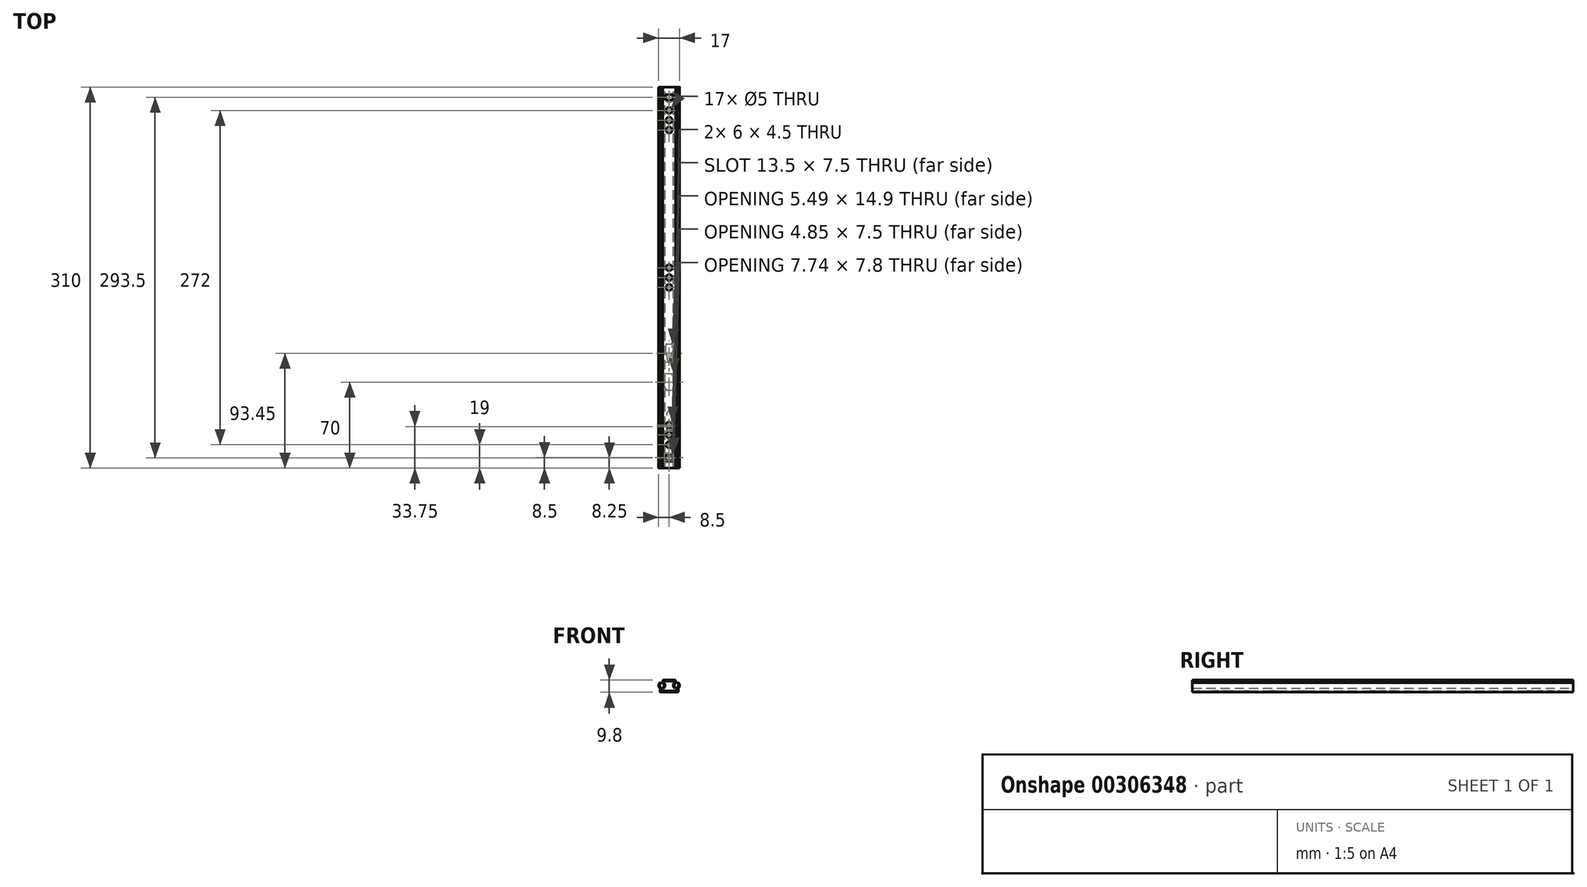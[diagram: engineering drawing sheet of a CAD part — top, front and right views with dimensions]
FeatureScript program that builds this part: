
annotation { "Feature Type Name" : "Feature", "Feature Type Description" : "" }
export const myFeature = defineFeature(function(context is Context, id is Id, definition is map)
    precondition{}
    {
        {
            var Q0;
            Q0=qCreatedBy(makeId("Front.planeOp"),FACE);
            var sketch = newSketch(context, id + "F0", { "sketchPlane" : qUnion([Q0])});
            skLineSegment(sketch, "E0", {"start": v(0, 0) * mm, "end": v(6.95, 0) * mm});
            skLineSegment(sketch, "E1", {"start": v(7.45, 0.5) * mm, "end": v(7.45, 3.02) * mm});
            skLineSegment(sketch, "E2", {"start": v(6.55, 3.43) * mm, "end": v(6.55, 1.4) * mm});
            skLineSegment(sketch, "E3", {"start": v(6.05, 0.9) * mm, "end": v(0, 0.9) * mm});
            skLineSegment(sketch, "E4", {"start": v(0, 0) * mm, "end": v(0, 0.9) * mm, "construction": true});
            skArc(sketch, "E5", {"start": v(7.6, 3.38) * mm, "mid": v(8.5, 5.55) * mm, "end": v(7.56, 7.7) * mm});
            skArc(sketch, "E6", {"start": v(6.75, 3.83) * mm, "mid": v(7.6, 5.48) * mm, "end": v(6.81, 7.16) * mm});
            skLineSegment(sketch, "E7", {"start": v(7.33, 7.74) * mm, "end": v(6.85, 7.5) * mm});
            skLineSegment(sketch, "E8.MirrorCS", {"start": v(-7.33, 7.74) * mm, "end": v(-6.85, 7.5) * mm});
            skLineSegment(sketch, "E9.MirrorCS", {"start": v(-7.45, 0.5) * mm, "end": v(-7.45, 3.02) * mm});
            skLineSegment(sketch, "E10.MirrorCS", {"start": v(-6.55, 3.43) * mm, "end": v(-6.55, 1.4) * mm});
            skLineSegment(sketch, "E11.MirrorCS", {"start": v(-6.05, 0.9) * mm, "end": v(0, 0.9) * mm});
            skArc(sketch, "E12.MirrorCS", {"start": v(-7.6, 3.38) * mm, "mid": v(-8.5, 5.55) * mm, "end": v(-7.56, 7.7) * mm});
            skArc(sketch, "E13.MirrorCS", {"start": v(-6.75, 3.83) * mm, "mid": v(-7.6, 5.48) * mm, "end": v(-6.81, 7.16) * mm});
            skLineSegment(sketch, "E14.MirrorCS", {"start": v(0, 0) * mm, "end": v(-6.95, 0) * mm});
            skLineSegment(sketch, "E15", {"start": v(6.55, 3.7) * mm, "end": v(7.45, 3.24) * mm, "construction": true});
            skLineSegment(sketch, "E16", {"start": v(5.5, 5.52) * mm, "end": v(-5.5, 5.52) * mm, "construction": true});
            skLineSegment(sketch, "E17", {"start": v(6.55, 0.9) * mm, "end": v(7.45, 0.9) * mm, "construction": true});
            skLineSegment(sketch, "E18", {"start": v(7.6, 5.52) * mm, "end": v(8.5, 5.52) * mm, "construction": true});
            skPoint(sketch, "E19.visualSharp", {"position": v(6.55, 0.9) * mm});
            skArc(sketch, "E19.filletArc", {"start": v(6.05, 0.9) * mm, "mid": v(6.4, 1.05) * mm, "end": v(6.55, 1.4) * mm});
            skPoint(sketch, "E20.visualSharp", {"position": v(7.45, 0) * mm});
            skArc(sketch, "E20.filletArc", {"start": v(6.95, 0) * mm, "mid": v(7.3, 0.15) * mm, "end": v(7.45, 0.5) * mm});
            skPoint(sketch, "E21.visualSharp", {"position": v(-6.55, 0.9) * mm});
            skArc(sketch, "E21.filletArc", {"start": v(-6.55, 1.4) * mm, "mid": v(-6.4, 1.05) * mm, "end": v(-6.05, 0.9) * mm});
            skPoint(sketch, "E22.visualSharp", {"position": v(-7.45, 0) * mm});
            skArc(sketch, "E22.filletArc", {"start": v(-7.45, 0.5) * mm, "mid": v(-7.3, 0.15) * mm, "end": v(-6.95, 0) * mm});
            skPoint(sketch, "E23.visualSharp", {"position": v(7.45, 3.24) * mm});
            skArc(sketch, "E23.filletArc", {"start": v(7.6, 3.38) * mm, "mid": v(7.49, 3.21) * mm, "end": v(7.45, 3.02) * mm});
            skPoint(sketch, "E24.visualSharp", {"position": v(6.55, 3.7) * mm});
            skArc(sketch, "E24.filletArc", {"start": v(6.75, 3.83) * mm, "mid": v(6.6, 3.66) * mm, "end": v(6.55, 3.43) * mm});
            skPoint(sketch, "E25.visualSharp", {"position": v(-7.45, 3.24) * mm});
            skArc(sketch, "E25.filletArc", {"start": v(-7.45, 3.02) * mm, "mid": v(-7.49, 3.21) * mm, "end": v(-7.6, 3.38) * mm});
            skPoint(sketch, "E26.visualSharp", {"position": v(-6.55, 3.7) * mm});
            skArc(sketch, "E26.filletArc", {"start": v(-6.55, 3.43) * mm, "mid": v(-6.6, 3.66) * mm, "end": v(-6.75, 3.83) * mm});
            skPoint(sketch, "E27.visualSharp", {"position": v(6.55, 7.34) * mm});
            skArc(sketch, "E27.filletArc", {"start": v(6.85, 7.5) * mm, "mid": v(6.74, 7.33) * mm, "end": v(6.81, 7.16) * mm});
            skPoint(sketch, "E28.visualSharp", {"position": v(-6.55, 7.34) * mm});
            skArc(sketch, "E28.filletArc", {"start": v(-6.81, 7.16) * mm, "mid": v(-6.74, 7.33) * mm, "end": v(-6.85, 7.5) * mm});
            skPoint(sketch, "E29.visualSharp", {"position": v(7.45, 7.8) * mm});
            skArc(sketch, "E29.filletArc", {"start": v(7.56, 7.7) * mm, "mid": v(7.45, 7.76) * mm, "end": v(7.33, 7.74) * mm});
            skPoint(sketch, "E30.visualSharp", {"position": v(-7.45, 7.8) * mm});
            skArc(sketch, "E30.filletArc", {"start": v(-7.33, 7.74) * mm, "mid": v(-7.45, 7.76) * mm, "end": v(-7.56, 7.7) * mm});
            skLineSegment(sketch, "E31", {"start": v(0, 9.8) * mm, "end": v(4.75, 9.8) * mm});
            skLineSegment(sketch, "E32", {"start": v(5.25, 9.3) * mm, "end": v(5.25, 7.6) * mm});
            skArc(sketch, "E33", {"start": v(5.05, 7.2) * mm, "mid": v(4.2, 5.56) * mm, "end": v(4.99, 3.88) * mm});
            skLineSegment(sketch, "E34", {"start": v(4.47, 3.3) * mm, "end": v(4.95, 3.55) * mm});
            skLineSegment(sketch, "E35", {"start": v(4.35, 7.8) * mm, "end": v(5.25, 7.34) * mm, "construction": true});
            skLineSegment(sketch, "E36", {"start": v(4.35, 8.02) * mm, "end": v(4.35, 8.4) * mm});
            skLineSegment(sketch, "E37", {"start": v(3.85, 8.9) * mm, "end": v(0, 8.9) * mm});
            skLineSegment(sketch, "E38", {"start": v(3.3, 5.52) * mm, "end": v(5.5, 5.52) * mm, "construction": true});
            skLineSegment(sketch, "E39", {"start": v(4.35, 8.9) * mm, "end": v(5.25, 8.9) * mm, "construction": true});
            skLineSegment(sketch, "E40", {"start": v(0, 9.8) * mm, "end": v(0, 8.9) * mm, "construction": true});
            skLineSegment(sketch, "E41", {"start": v(3.3, 5.52) * mm, "end": v(4.2, 5.52) * mm, "construction": true});
            skArc(sketch, "E42", {"start": v(4.2, 7.66) * mm, "mid": v(3.3, 5.49) * mm, "end": v(4.24, 3.33) * mm});
            skPoint(sketch, "E43.visualSharp", {"position": v(4.35, 8.9) * mm});
            skArc(sketch, "E43.filletArc", {"start": v(4.35, 8.4) * mm, "mid": v(4.2, 8.75) * mm, "end": v(3.85, 8.9) * mm});
            skPoint(sketch, "E44.visualSharp", {"position": v(5.25, 9.8) * mm});
            skArc(sketch, "E44.filletArc", {"start": v(5.25, 9.3) * mm, "mid": v(5.1, 9.65) * mm, "end": v(4.75, 9.8) * mm});
            skPoint(sketch, "E45.visualSharp", {"position": v(5.25, 7.34) * mm});
            skArc(sketch, "E45.filletArc", {"start": v(5.05, 7.2) * mm, "mid": v(5.2, 7.38) * mm, "end": v(5.25, 7.6) * mm});
            skPoint(sketch, "E46.visualSharp", {"position": v(4.35, 7.8) * mm});
            skArc(sketch, "E46.filletArc", {"start": v(4.2, 7.66) * mm, "mid": v(4.31, 7.83) * mm, "end": v(4.35, 8.02) * mm});
            skPoint(sketch, "E47.visualSharp", {"position": v(5.25, 3.7) * mm});
            skArc(sketch, "E47.filletArc", {"start": v(4.95, 3.55) * mm, "mid": v(5.06, 3.7) * mm, "end": v(4.99, 3.88) * mm});
            skPoint(sketch, "E48.visualSharp", {"position": v(4.35, 3.24) * mm});
            skArc(sketch, "E48.filletArc", {"start": v(4.24, 3.33) * mm, "mid": v(4.35, 3.28) * mm, "end": v(4.47, 3.3) * mm});
            skArc(sketch, "E49.MirrorCS", {"start": v(-4.2, 7.66) * mm, "mid": v(-4.31, 7.83) * mm, "end": v(-4.35, 8.02) * mm});
            skArc(sketch, "E50.MirrorCS", {"start": v(-4.24, 3.33) * mm, "mid": v(-4.35, 3.28) * mm, "end": v(-4.47, 3.3) * mm});
            skLineSegment(sketch, "E51.MirrorCS", {"start": v(-4.35, 8.02) * mm, "end": v(-4.35, 8.4) * mm});
            skArc(sketch, "E52.MirrorCS", {"start": v(-4.35, 8.4) * mm, "mid": v(-4.2, 8.75) * mm, "end": v(-3.85, 8.9) * mm});
            skArc(sketch, "E53.MirrorCS", {"start": v(-4.95, 3.55) * mm, "mid": v(-5.06, 3.7) * mm, "end": v(-4.99, 3.88) * mm});
            skLineSegment(sketch, "E54.MirrorCS", {"start": v(-4.47, 3.3) * mm, "end": v(-4.95, 3.55) * mm});
            skArc(sketch, "E55.MirrorCS", {"start": v(-5.05, 7.2) * mm, "mid": v(-5.2, 7.38) * mm, "end": v(-5.25, 7.6) * mm});
            skLineSegment(sketch, "E56.MirrorCS", {"start": v(-4.35, 7.8) * mm, "end": v(-5.25, 7.34) * mm, "construction": true});
            skArc(sketch, "E57.MirrorCS", {"start": v(-5.25, 9.3) * mm, "mid": v(-5.1, 9.65) * mm, "end": v(-4.75, 9.8) * mm});
            skLineSegment(sketch, "E58.MirrorCS", {"start": v(-3.3, 5.52) * mm, "end": v(-4.2, 5.52) * mm, "construction": true});
            skArc(sketch, "E59.MirrorCS", {"start": v(-4.2, 7.66) * mm, "mid": v(-3.3, 5.49) * mm, "end": v(-4.24, 3.33) * mm});
            skPoint(sketch, "E60.MirrorP", {"position": v(-4.35, 3.24) * mm});
            skPoint(sketch, "E61.MirrorP", {"position": v(-5.25, 7.34) * mm});
            skLineSegment(sketch, "E62.MirrorCS", {"start": v(-4.35, 8.9) * mm, "end": v(-5.25, 8.9) * mm, "construction": true});
            skPoint(sketch, "E63.MirrorP", {"position": v(-4.35, 8.9) * mm});
            skPoint(sketch, "E64.MirrorP", {"position": v(-5.25, 9.8) * mm});
            skLineSegment(sketch, "E65.MirrorCS", {"start": v(0, 9.8) * mm, "end": v(-4.75, 9.8) * mm});
            skPoint(sketch, "E66.MirrorP", {"position": v(-4.35, 7.8) * mm});
            skArc(sketch, "E67.MirrorCS", {"start": v(-5.05, 7.2) * mm, "mid": v(-4.2, 5.56) * mm, "end": v(-4.99, 3.88) * mm});
            skPoint(sketch, "E68.MirrorP", {"position": v(-5.25, 3.7) * mm});
            skLineSegment(sketch, "E69.MirrorCS", {"start": v(-3.85, 8.9) * mm, "end": v(0, 8.9) * mm});
            skLineSegment(sketch, "E70.MirrorCS", {"start": v(-5.25, 9.3) * mm, "end": v(-5.25, 7.6) * mm});
            skLineSegment(sketch, "E71.MirrorCS", {"start": v(-3.3, 5.52) * mm, "end": v(-5.5, 5.52) * mm, "construction": true});
            skSolve(sketch);
        }
        {
            var Q0;
            Q0=makeQuery(id+"F0.imprint","IMPRINT",FACE,{"disambiguationData":[TD([[makeQuery(id+"F0.imprint","IMPRINT",EDGE,{"derivedFrom":sQuery(id+"F0.wireOp",EDGE,"E0")}),1.0]])]});
            extrude(context, id + "F1", {"entities" : qUnion([Q0]), "depth" : 310 * mm});
        }
        {
            var Q0;
            Q0=makeQuery(id+"F1.opExtrude","SWEPT_FACE",FACE,{"disambiguationData":[OSD([sQuery(id+"F0.wireOp",EDGE,"E0"),sQuery(id+"F0.wireOp",EDGE,"E14.MirrorCS")])]});
            var sketch = newSketch(context, id + "F2", { "sketchPlane" : qUnion([Q0])});
            skLineSegment(sketch, "E72", {"start": v(0, 310) * mm, "end": v(0, 0) * mm, "construction": true});
            skLineSegment(sketch, "E73", {"start": v(0, 155) * mm, "end": v(-6.95, 155) * mm, "construction": true});
            skCircle(sketch, "E74", {"center": v(0, 10) * mm, "radius": 2.65 * mm});
            skCircle(sketch, "E75", {"center": v(0, 301.5) * mm, "radius": 3.9 * mm});
            skCircle(sketch, "E76", {"center": v(0, 278) * mm, "radius": 2 * mm});
            skCircle(sketch, "E77", {"center": v(0, 266) * mm, "radius": 2 * mm});
            skLineSegment(sketch, "E78", {"start": v(0, 243) * mm, "end": v(0, 237) * mm});
            skArc(sketch, "E79.0.startCap", {"start": v(-3.75, 243) * mm, "mid": v(0, 246.75) * mm, "end": v(3.75, 243) * mm});
            skArc(sketch, "E79.0.endCap", {"start": v(3.75, 237) * mm, "mid": v(0, 233.25) * mm, "end": v(-3.75, 237) * mm});
            skLineSegment(sketch, "E79.0.left", {"start": v(3.75, 243) * mm, "end": v(3.75, 237) * mm});
            skLineSegment(sketch, "E79.0.right", {"start": v(-3.75, 243) * mm, "end": v(-3.75, 237) * mm});
            skArc(sketch, "E80", {"start": v(0, 224) * mm, "mid": v(0.66, 223.75) * mm, "end": v(1, 223.13) * mm});
            skLineSegment(sketch, "E81", {"start": v(1, 223.13) * mm, "end": v(2.74, 210.23) * mm});
            skLineSegment(sketch, "E82", {"start": v(1.75, 209.1) * mm, "end": v(0, 209.1) * mm});
            skArc(sketch, "E83.MirrorCS", {"start": v(0, 224) * mm, "mid": v(-0.66, 223.75) * mm, "end": v(-1, 223.13) * mm});
            skLineSegment(sketch, "E84.MirrorCS", {"start": v(-1, 223.13) * mm, "end": v(-2.74, 210.23) * mm});
            skLineSegment(sketch, "E85.MirrorCS", {"start": v(-1.75, 209.1) * mm, "end": v(0, 209.1) * mm});
            skPoint(sketch, "E86.visualSharp", {"position": v(2.9, 209.1) * mm});
            skArc(sketch, "E86.filletArc", {"start": v(1.75, 209.1) * mm, "mid": v(2.5, 209.44) * mm, "end": v(2.74, 210.23) * mm});
            skPoint(sketch, "E87.visualSharp", {"position": v(-2.9, 209.1) * mm});
            skArc(sketch, "E87.filletArc", {"start": v(-2.74, 210.23) * mm, "mid": v(-2.5, 209.44) * mm, "end": v(-1.75, 209.1) * mm});
            skSolve(sketch);
        }
        {
            var Q0;
            Q0 = qSketchRegion(id + "F2", true);
            extrude(context, id + "F3", {"entities" : qUnion([Q0]), "operationType" : NewBodyOperationType.REMOVE, "oppositeDirection" : true, "depth" : 25 * mm});
        }
        {
            var Q0;
            Q0=makeQuery(id+"F0.imprint","IMPRINT",FACE,{"disambiguationData":[TD([[makeQuery(id+"F0.imprint","IMPRINT",EDGE,{"derivedFrom":sQuery(id+"F0.wireOp",EDGE,"E31")}),-1.0]])]});
            var Q1;
            Q1=makeQuery(id+"F1.opExtrude","CAP_FACE",FACE,{"disambiguationData":[OSD([sQuery(id+"F0.wireOp",EDGE,"E0"),sQuery(id+"F0.wireOp",EDGE,"E1"),sQuery(id+"F0.wireOp",EDGE,"E2"),sQuery(id+"F0.wireOp",EDGE,"E3"),sQuery(id+"F0.wireOp",EDGE,"E5"),sQuery(id+"F0.wireOp",EDGE,"E6"),sQuery(id+"F0.wireOp",EDGE,"E7"),sQuery(id+"F0.wireOp",EDGE,"E8.MirrorCS"),sQuery(id+"F0.wireOp",EDGE,"E9.MirrorCS"),sQuery(id+"F0.wireOp",EDGE,"E10.MirrorCS"),sQuery(id+"F0.wireOp",EDGE,"E11.MirrorCS"),sQuery(id+"F0.wireOp",EDGE,"E12.MirrorCS"),sQuery(id+"F0.wireOp",EDGE,"E13.MirrorCS"),sQuery(id+"F0.wireOp",EDGE,"E14.MirrorCS"),sQuery(id+"F0.wireOp",EDGE,"E19.filletArc"),sQuery(id+"F0.wireOp",EDGE,"E20.filletArc"),sQuery(id+"F0.wireOp",EDGE,"E21.filletArc"),sQuery(id+"F0.wireOp",EDGE,"E22.filletArc"),sQuery(id+"F0.wireOp",EDGE,"E23.filletArc"),sQuery(id+"F0.wireOp",EDGE,"E24.filletArc"),sQuery(id+"F0.wireOp",EDGE,"E25.filletArc"),sQuery(id+"F0.wireOp",EDGE,"E26.filletArc"),sQuery(id+"F0.wireOp",EDGE,"E27.filletArc"),sQuery(id+"F0.wireOp",EDGE,"E28.filletArc"),sQuery(id+"F0.wireOp",EDGE,"E29.filletArc"),sQuery(id+"F0.wireOp",EDGE,"E30.filletArc")])],"isStart":false});
            extrude(context, id + "F4", {"entities" : qUnion([Q0]), "endBound" : BoundingType.UP_TO_SURFACE, "endBoundEntityFace" : qUnion([Q1]), "depth" : 25 * mm});
        }
        {
            var Q0;
            Q0=makeQuery(id+"F4.opExtrude","SWEPT_FACE",FACE,{"disambiguationData":[OSD([sQuery(id+"F0.wireOp",EDGE,"E31"),sQuery(id+"F0.wireOp",EDGE,"E65.MirrorCS")])]});
            var sketch = newSketch(context, id + "F5", { "sketchPlane" : qUnion([Q0])});
            skLineSegment(sketch, "E88", {"start": v(0, -310) * mm, "end": v(0, 0) * mm, "construction": true});
            skCircle(sketch, "E89", {"center": v(0, -19) * mm, "radius": 2.5 * mm});
            skCircle(sketch, "E90.1.0.0", {"center": v(0, -27) * mm, "radius": 2.5 * mm});
            skCircle(sketch, "E90.2.0.0", {"center": v(0, -35) * mm, "radius": 2.5 * mm});
            skLineSegment(sketch, "E90.direction1", {"start": v(0, -19) * mm, "end": v(0, -27) * mm, "construction": true});
            skLineSegment(sketch, "E91.bottom", {"start": v(-3, -6) * mm, "end": v(3, -6) * mm});
            skLineSegment(sketch, "E91.top", {"start": v(-3, -10.5) * mm, "end": v(3, -10.5) * mm});
            skLineSegment(sketch, "E91.left", {"start": v(-3, -6) * mm, "end": v(-3, -10.5) * mm});
            skLineSegment(sketch, "E91.right", {"start": v(3, -6) * mm, "end": v(3, -10.5) * mm});
            skPoint(sketch, "E91.middle", {"position": v(0, -8.25) * mm});
            skLineSegment(sketch, "E92", {"start": v(0, -155) * mm, "end": v(128.23, -155) * mm, "construction": true});
            skPoint(sketch, "E92.endSnap0", {"position": v(0, -155) * mm});
            skCircle(sketch, "E93.MirrorC", {"center": v(0, -283) * mm, "radius": 2.5 * mm});
            skCircle(sketch, "E94.MirrorC", {"center": v(0, -291) * mm, "radius": 2.5 * mm});
            skCircle(sketch, "E95.MirrorC", {"center": v(0, -275) * mm, "radius": 2.5 * mm});
            skCircle(sketch, "E96.1.0.0", {"center": v(0, -163) * mm, "radius": 2.5 * mm});
            skCircle(sketch, "E96.1.0.1", {"center": v(0, -155) * mm, "radius": 2.5 * mm});
            skCircle(sketch, "E96.1.0.2", {"center": v(0, -147) * mm, "radius": 2.5 * mm});
            skLineSegment(sketch, "E96.direction1", {"start": v(0, -35) * mm, "end": v(0, -163) * mm, "construction": true});
            skPoint(sketch, "E97.MirrorP", {"position": v(0, -301.75) * mm});
            skLineSegment(sketch, "E98.MirrorCS", {"start": v(-3, -299.5) * mm, "end": v(3, -299.5) * mm});
            skLineSegment(sketch, "E99.MirrorCS", {"start": v(3, -304) * mm, "end": v(3, -299.5) * mm});
            skLineSegment(sketch, "E100.MirrorCS", {"start": v(-3, -304) * mm, "end": v(-3, -299.5) * mm});
            skLineSegment(sketch, "E101.MirrorCS", {"start": v(-3, -304) * mm, "end": v(3, -304) * mm});
            skSolve(sketch);
        }
        {
            var Q0;
            Q0 = qSketchRegion(id + "F5", true);
            extrude(context, id + "F6", {"entities" : qUnion([Q0]), "operationType" : NewBodyOperationType.REMOVE, "oppositeDirection" : true, "depth" : 25 * mm});
        }
    });
